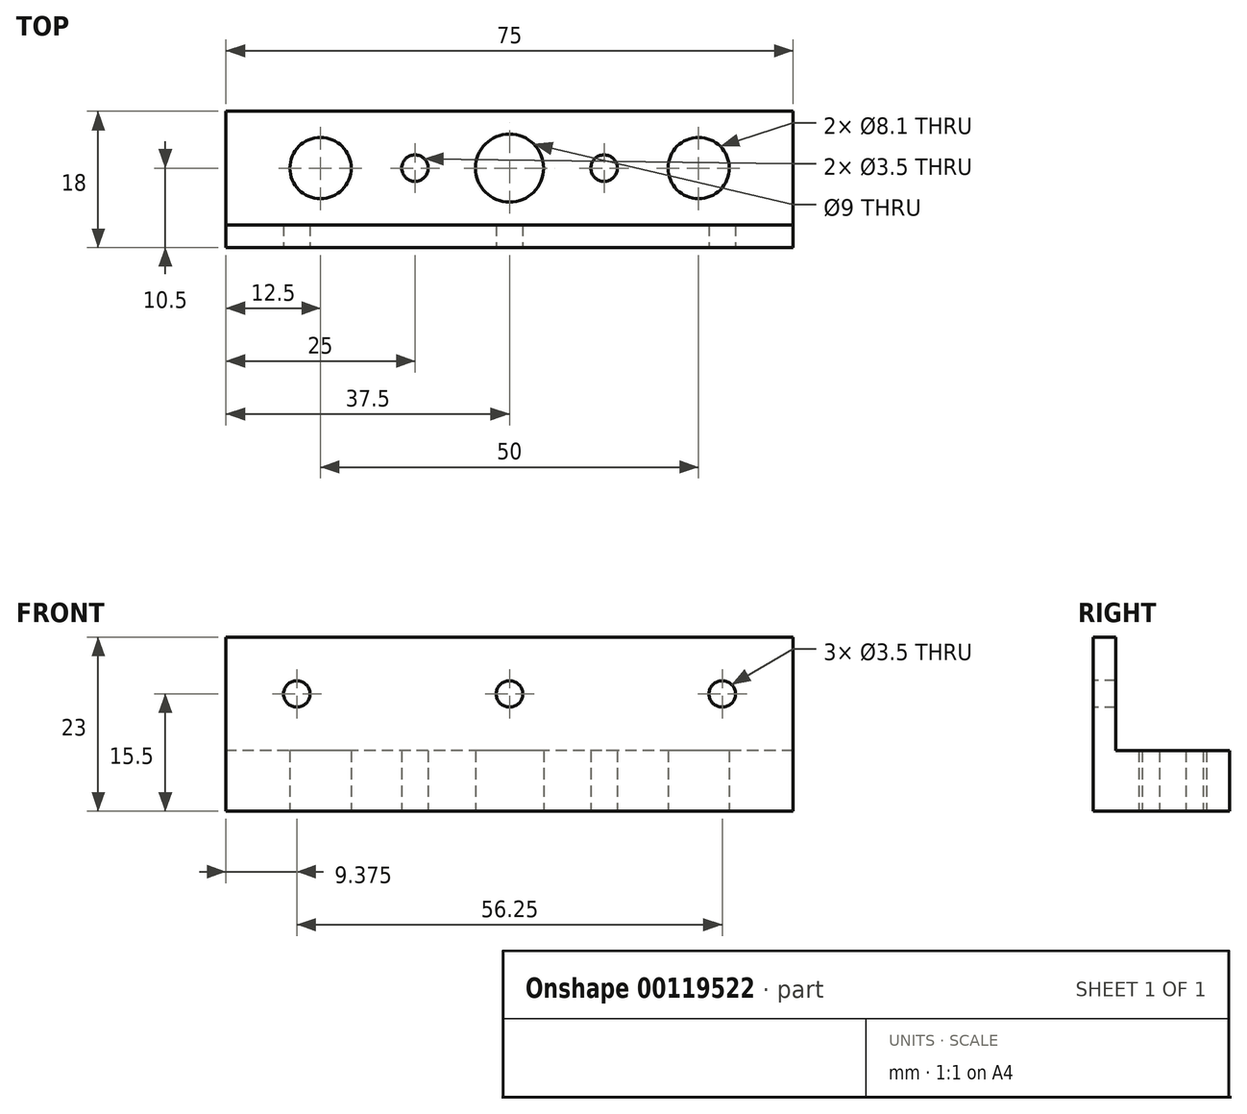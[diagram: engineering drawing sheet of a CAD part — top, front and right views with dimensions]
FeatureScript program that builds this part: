
annotation { "Feature Type Name" : "Feature", "Feature Type Description" : "" }
export const myFeature = defineFeature(function(context is Context, id is Id, definition is map)
    precondition{}
    {
        {
            var Q0;
            Q0=qCreatedBy(makeId("Top.planeOp"),FACE);
            var sketch = newSketch(context, id + "F0", { "sketchPlane" : qUnion([Q0])});
            skLineSegment(sketch, "E0.bottom", {"start": v(37.5, -7.5) * mm, "end": v(-37.5, -7.5) * mm});
            skLineSegment(sketch, "E0.top", {"start": v(37.5, 7.5) * mm, "end": v(-37.5, 7.5) * mm});
            skLineSegment(sketch, "E0.left", {"start": v(37.5, -7.5) * mm, "end": v(37.5, 7.5) * mm});
            skLineSegment(sketch, "E0.right", {"start": v(-37.5, -7.5) * mm, "end": v(-37.5, 7.5) * mm});
            skPoint(sketch, "E0.middle", {"position": v(0, 0) * mm});
            skCircle(sketch, "E1", {"center": v(0, 0) * mm, "radius": 4.5 * mm});
            skPoint(sketch, "E2.middle", {"position": v(0, 7.5) * mm});
            skLineSegment(sketch, "E3", {"start": v(-37.5, 0) * mm, "end": v(-25, 0) * mm, "construction": true});
            skPoint(sketch, "E3.endSnap0", {"position": v(-37.5, 0) * mm});
            skLineSegment(sketch, "E4", {"start": v(37.5, 0) * mm, "end": v(25, 0) * mm, "construction": true});
            skCircle(sketch, "E5", {"center": v(-25, 0) * mm, "radius": 4.05 * mm});
            skCircle(sketch, "E6", {"center": v(25, 0) * mm, "radius": 4.05 * mm});
            skLineSegment(sketch, "E7.bottom", {"start": v(-37.5, 7.5) * mm, "end": v(37.5, 7.5) * mm});
            skLineSegment(sketch, "E7.top", {"start": v(-37.5, 10.5) * mm, "end": v(37.5, 10.5) * mm});
            skLineSegment(sketch, "E7.left", {"start": v(-37.5, 7.5) * mm, "end": v(-37.5, 10.5) * mm});
            skLineSegment(sketch, "E7.right", {"start": v(37.5, 7.5) * mm, "end": v(37.5, 10.5) * mm});
            skLineSegment(sketch, "E8.top", {"start": v(37.5, -10.5) * mm, "end": v(-37.5, -10.5) * mm});
            skLineSegment(sketch, "E8.left", {"start": v(37.5, -7.5) * mm, "end": v(37.5, -10.5) * mm});
            skLineSegment(sketch, "E8.right", {"start": v(-37.5, -7.5) * mm, "end": v(-37.5, -10.5) * mm});
            skLineSegment(sketch, "E9", {"start": v(-25, 0) * mm, "end": v(0, 0) * mm, "construction": true});
            skLineSegment(sketch, "E10", {"start": v(0, 0) * mm, "end": v(25, 0) * mm, "construction": true});
            skCircle(sketch, "E11", {"center": v(-12.5, 0) * mm, "radius": 1.75 * mm});
            skCircle(sketch, "E12", {"center": v(12.5, 0) * mm, "radius": 1.75 * mm});
            skSolve(sketch);
        }
        {
            var Q0;
            Q0=makeQuery(id+"F0.imprint","IMPRINT",FACE,{"disambiguationData":[TD([[makeQuery(id+"F0.imprint","IMPRINT",EDGE,{"derivedFrom":sQuery(id+"F0.wireOp",EDGE,"E0.left")}),1.0]])]});
            extrude(context, id + "F1", {"entities" : qUnion([Q0]), "depth" : 8 * mm});
        }
        {
            var Q0;
            Q0=makeQuery(id+"F0.imprint","IMPRINT",FACE,{"disambiguationData":[TD([[makeQuery(id+"F0.imprint","IMPRINT",EDGE,{"derivedFrom":sQuery(id+"F0.wireOp",EDGE,"E7.bottom")}),1.0]])]});
            var Q1;
            Q1=makeQuery(id+"F0.imprint","IMPRINT",FACE,{"disambiguationData":[TD([[makeQuery(id+"F0.imprint","IMPRINT",EDGE,{"derivedFrom":sQuery(id+"F0.wireOp",EDGE,"E0.bottom")}),1.0]])]});
            extrude(context, id + "F2", {"entities" : qUnion([Q0, Q1]), "operationType" : NewBodyOperationType.ADD, "depth" : 23 * mm});
        }
        {
            var Q0;
            Q0=makeQuery(id+"F2.opExtrude","SWEPT_FACE",FACE,{"disambiguationData":[OSD([sQuery(id+"F0.wireOp",EDGE,"E8.top")])]});
            var sketch = newSketch(context, id + "F3", { "sketchPlane" : qUnion([Q0])});
            skLineSegment(sketch, "E13.bottom", {"start": v(-37.5, 23) * mm, "end": v(37.5, 23) * mm, "construction": true});
            skLineSegment(sketch, "E13.top", {"start": v(-37.5, 8) * mm, "end": v(37.5, 8) * mm, "construction": true});
            skLineSegment(sketch, "E13.left", {"start": v(-37.5, 23) * mm, "end": v(-37.5, 8) * mm, "construction": true});
            skLineSegment(sketch, "E13.right", {"start": v(37.5, 23) * mm, "end": v(37.5, 8) * mm, "construction": true});
            skLineSegment(sketch, "E14", {"start": v(0, 15.5) * mm, "end": v(-37.5, 15.5) * mm, "construction": true});
            skPoint(sketch, "E14.startSnap0", {"position": v(-37.5, 15.5) * mm});
            skLineSegment(sketch, "E15", {"start": v(0, 15.5) * mm, "end": v(37.5, 15.5) * mm, "construction": true});
            skCircle(sketch, "E16", {"center": v(0, 15.5) * mm, "radius": 1.75 * mm});
            skLineSegment(sketch, "E17", {"start": v(-18.75, 18.1) * mm, "end": v(-37.5, 18.1) * mm, "construction": true});
            skPoint(sketch, "E17.startSnap0", {"position": v(-18.75, 15.5) * mm});
            skLineSegment(sketch, "E18", {"start": v(-28.12, 18.1) * mm, "end": v(-28.12, 8) * mm, "construction": true});
            skLineSegment(sketch, "E19", {"start": v(18.75, 18.1) * mm, "end": v(37.5, 18.1) * mm, "construction": true});
            skPoint(sketch, "E19.startSnap0", {"position": v(18.75, 15.5) * mm});
            skLineSegment(sketch, "E20", {"start": v(28.12, 18.1) * mm, "end": v(28.12, 8) * mm, "construction": true});
            skCircle(sketch, "E21", {"center": v(-28.12, 15.5) * mm, "radius": 1.75 * mm});
            skCircle(sketch, "E22", {"center": v(28.12, 15.5) * mm, "radius": 1.75 * mm});
            skSolve(sketch);
        }
        {
            var Q0;
            Q0=makeQuery(id+"F3.imprint","IMPRINT",FACE,{"disambiguationData":[TD([[makeQuery(id+"F3.imprint","IMPRINT",EDGE,{"derivedFrom":sQuery(id+"F3.wireOp",EDGE,"E21")}),1.0]])]});
            var Q1;
            Q1=makeQuery(id+"F3.imprint","IMPRINT",FACE,{"disambiguationData":[TD([[makeQuery(id+"F3.imprint","IMPRINT",EDGE,{"derivedFrom":sQuery(id+"F3.wireOp",EDGE,"E16")}),1.0]])]});
            var Q2;
            Q2=makeQuery(id+"F3.imprint","IMPRINT",FACE,{"disambiguationData":[TD([[makeQuery(id+"F3.imprint","IMPRINT",EDGE,{"derivedFrom":sQuery(id+"F3.wireOp",EDGE,"E22")}),1.0]])]});
            extrude(context, id + "F4", {"entities" : qUnion([Q0, Q1, Q2]), "operationType" : NewBodyOperationType.REMOVE, "oppositeDirection" : true, "depth" : 25 * mm});
        }
    });
